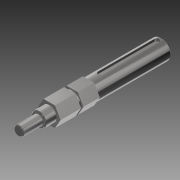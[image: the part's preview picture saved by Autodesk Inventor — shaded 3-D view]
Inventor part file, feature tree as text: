
AUTODESK INVENTOR PART (.ipt)
format: ipt  version: 2014 (Build 180170000, 170)  size: 133,632 bytes
history: native  units: mm
features: sketch x2, imported_body x1, extrude x1, hole x1
ambient origin geometry x8: Origin, YZ Plane, XZ Plane, XY Plane, X Axis, Y Axis, Z Axis, Center Point
bodies: Solid1 (feature_tree)
feature tree (5):
  imported_body  "Base1"
  extrude  "Extrusion1"  [1 undecoded]
  hole  "Hole1"  [1 undecoded]
  sketch  "Sketch1"  dims[d0=38.599999mm d1=0.0mm]
  sketch  "Sketch2"  dims[d2=4.9784mm d3=19.05mm d4=9.525mm d5=6.35mm d6=14.3117mm d7=25.4mm d8=20.594885mm]
note: 2 required parameter values undecoded (feature->parameter linkage not recoverable at this tier; creation-order binding heuristic only, values carry confidence <= 0.55)
